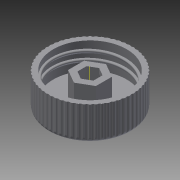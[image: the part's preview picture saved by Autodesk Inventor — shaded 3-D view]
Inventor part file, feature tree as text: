
AUTODESK INVENTOR PART (.ipt)
format: ipt  version: 2015 SP1 (Build 190203100, 203)  size: 541,696 bytes
history: native  units: mm
features: sketch x7, extrude x6, other x2, fillet x2, projected_geometry x2, pattern_circular x1
ambient origin geometry x8: Origin, YZ Plane, XZ Plane, XY Plane, X Axis, Y Axis, Z Axis, Center Point
bodies: Body1 (feature_tree), Body2 (feature_tree), Body3 (feature_tree), Body4 (feature_tree), Body5 (feature_tree), Body6 (feature_tree)
feature tree (20):
  other  "Sólido1"
  extrude  "Extrusión1"  Depth=32.0mm
  extrude  "Extrusión2"  Depth=28.0mm
  other  "Bobina1"
  extrude  "Extrusión3"  Depth=10.0mm
  extrude  "Extrusión4"  Depth=10.0mm TaperAngle=0.0deg
  extrude  "Extrusión5"  Depth=2.0mm
  fillet  "Empalme1"  Radius=2.0mm
  fillet  "Empalme2"  Radius=1.3mm
  extrude  "Extrusión6"  TaperAngle=90.0deg  [1 undecoded]
  pattern_circular  "Patrón circular1"  [2 undecoded]
  sketch  "Boceto1"  dims[d0=28.0mm d1=32.0mm]
  sketch  "Boceto2"  dims[d2=3.0mm d3=0.0mm d4=28.0mm]
  sketch  "Boceto3"  dims[d5=10.0mm d6=0.0mm]
  projected_geometry  "Contorno proyectado1"
  sketch  "Boceto4"  dims[d11=3.0mm d12=10.0mm d13=14.0mm d14=0.0mm d15=90.0deg d16=90.0deg d17=0.0mm d18=0.0mm d19=9.12mm]
  sketch  "Boceto5"  dims[d20=10.0mm d21=0.0mm d22=7.0mm d23=0.0mm]
  sketch  "Boceto6"  dims[d24=2.0mm d25=0.0mm d26=2.0mm d28=2.0mm d29=1.3mm]
  sketch  "Boceto7"  dims[d30=1.5mm d31=90.0deg d32=0.35mm d33=9.12mm d34=7.0mm d35=177.0mm d36=0.0mm d37=600.0mm d38=360.0deg]
  projected_geometry  "Contorno proyectado3"
note: 3 required parameter values undecoded (feature->parameter linkage not recoverable at this tier; creation-order binding heuristic only, values carry confidence <= 0.55)
